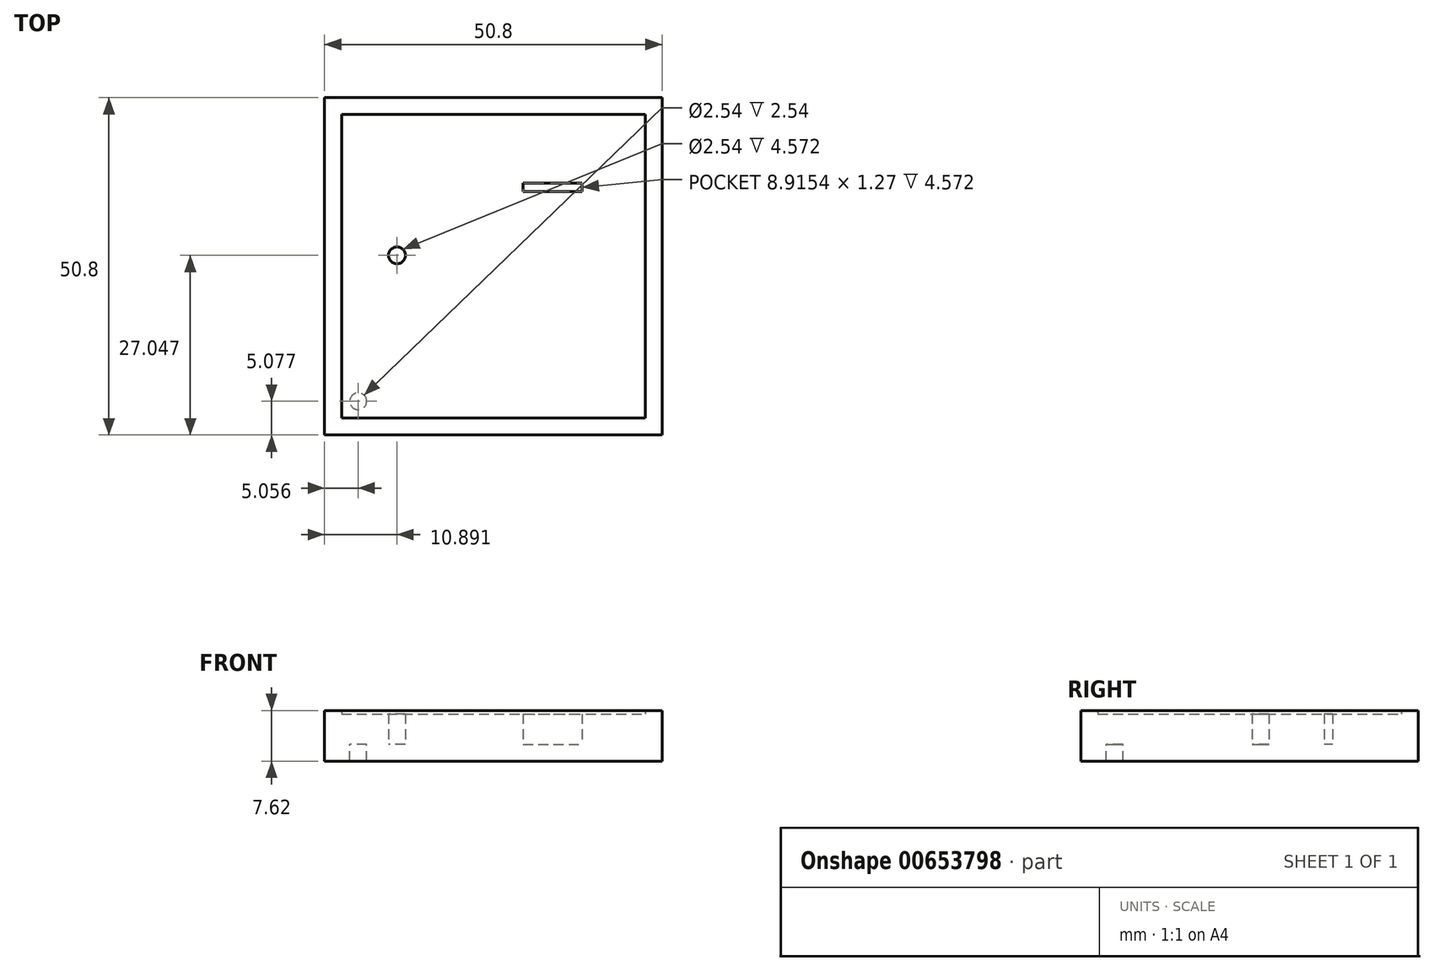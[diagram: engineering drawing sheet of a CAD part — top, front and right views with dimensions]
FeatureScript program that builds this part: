
annotation { "Feature Type Name" : "Feature", "Feature Type Description" : "" }
export const myFeature = defineFeature(function(context is Context, id is Id, definition is map)
    precondition{}
    {
        {
            var Q0;
            Q0=qCreatedBy(makeId("Top.planeOp"),FACE);
            var sketch = newSketch(context, id + "F0", { "sketchPlane" : qUnion([Q0])});
            skLineSegment(sketch, "E0.bottom", {"start": v(0, 0) * mm, "end": v(50.8, 0) * mm});
            skLineSegment(sketch, "E0.top", {"start": v(0, 50.8) * mm, "end": v(50.8, 50.8) * mm});
            skLineSegment(sketch, "E0.left", {"start": v(0, 0) * mm, "end": v(0, 50.8) * mm});
            skLineSegment(sketch, "E0.right", {"start": v(50.8, 0) * mm, "end": v(50.8, 50.8) * mm});
            skSolve(sketch);
        }
        {
            var Q0;
            Q0=makeQuery(id+"F0.imprint","IMPRINT",FACE,{"disambiguationData":[TD([[makeQuery(id+"F0.imprint","IMPRINT",EDGE,{"derivedFrom":sQuery(id+"F0.wireOp",EDGE,"E0.bottom")}),1.0]])]});
            extrude(context, id + "F1", {"entities" : qUnion([Q0]), "depth" : 7.62 * mm, "offsetDistance" : 25.4 * mm});
        }
        {
            var Q0;
            Q0=makeQuery(id+"F1.opExtrude","CAP_FACE",FACE,{"disambiguationData":[OSD([sQuery(id+"F0.wireOp",EDGE,"E0.bottom"),sQuery(id+"F0.wireOp",EDGE,"E0.top"),sQuery(id+"F0.wireOp",EDGE,"E0.left"),sQuery(id+"F0.wireOp",EDGE,"E0.right")])],"isStart":false});
            shell(context, id + "F2", {"entities" : qUnion([Q0]), "thickness" : 2.54 * mm});
        }
        {
            var Q0;
            Q0=makeQuery(id+"F2.opShell","OFFSET_FACE",FACE,{"disambiguationData":[OSD([sQuery(id+"F0.wireOp",EDGE,"E0.bottom"),sQuery(id+"F0.wireOp",EDGE,"E0.top"),sQuery(id+"F0.wireOp",EDGE,"E0.left"),sQuery(id+"F0.wireOp",EDGE,"E0.right")])]});
            var sketch = newSketch(context, id + "F3", { "sketchPlane" : qUnion([Q0])});
            skLineSegment(sketch, "E1", {"start": v(2.54, 2.54) * mm, "end": v(7.62, 2.54) * mm});
            skSolve(sketch);
        }
        {
            var Q0;
            {var subQ6=sQuery(id+"F3.wireOp",EDGE,"E1");Q0=makeQuery(id+"F3.imprint","IMPRINT",FACE,{"disambiguationData":[TD([[makeQuery(id+"F3.imprint","IMPRINT",EDGE,{"derivedFrom":subQ6}),1.0]])]});}
            var sketch = newSketch(context, id + "F4", { "sketchPlane" : qUnion([Q0])});
            skLineSegment(sketch, "E2", {"start": v(2.52, 2.54) * mm, "end": v(5.06, 2.54) * mm});
            skLineSegment(sketch, "E3", {"start": v(5.06, 2.54) * mm, "end": v(5.06, 5.08) * mm});
            skLineSegment(sketch, "E4", {"start": v(5.06, 5.08) * mm, "end": v(2.52, 5.08) * mm});
            skCircle(sketch, "E5", {"center": v(5.06, 5.08) * mm, "radius": 1.27 * mm});
            skSolve(sketch);
        }
        {
            var Q0;
            Q0 = qSketchRegion(id + "F4", true);
            extrude(context, id + "F5", {"entities" : qUnion([Q0]), "operationType" : NewBodyOperationType.REMOVE, "oppositeDirection" : true, "depth" : 25.4 * mm, "offsetDistance" : 25.4 * mm});
        }
        {
            var Q0;
            {var subQ6=sQuery(id+"F3.wireOp",EDGE,"E1");Q0=makeQuery(id+"F3.imprint","IMPRINT",FACE,{"disambiguationData":[TD([[makeQuery(id+"F3.imprint","IMPRINT",EDGE,{"derivedFrom":subQ6}),1.0]])]});}
            var sketch = newSketch(context, id + "F6", { "sketchPlane" : qUnion([Q0])});
            skLineSegment(sketch, "E6.bottom", {"start": v(29.87, 37.92) * mm, "end": v(38.79, 37.92) * mm});
            skLineSegment(sketch, "E6.top", {"start": v(29.87, 36.65) * mm, "end": v(38.79, 36.65) * mm});
            skLineSegment(sketch, "E6.left", {"start": v(29.87, 37.92) * mm, "end": v(29.87, 36.65) * mm});
            skLineSegment(sketch, "E6.right", {"start": v(38.79, 37.92) * mm, "end": v(38.79, 36.65) * mm});
            skSolve(sketch);
        }
        {
            var Q0;
            Q0=makeQuery(id+"F6.imprint","IMPRINT",FACE,{"disambiguationData":[TD([[makeQuery(id+"F6.imprint","IMPRINT",EDGE,{"derivedFrom":sQuery(id+"F6.wireOp",EDGE,"E6.bottom")}),1.0]])]});
            var sketch = newSketch(context, id + "F7", { "sketchPlane" : qUnion([Q0])});
            skCircle(sketch, "E7", {"center": v(10.9, 27.05) * mm, "radius": 1.27 * mm});
            skSolve(sketch);
        }
        {
            var Q0;
            Q0=makeQuery(id+"F7.imprint","IMPRINT",FACE,{"disambiguationData":[TD([[makeQuery(id+"F7.imprint","IMPRINT",EDGE,{"derivedFrom":sQuery(id+"F7.wireOp",EDGE,"E7")}),-1.0]])]});
            extrude(context, id + "F8", {"entities" : qUnion([Q0]), "operationType" : NewBodyOperationType.ADD, "depth" : 4.57 * mm, "offsetDistance" : 25.4 * mm});
        }
    });
